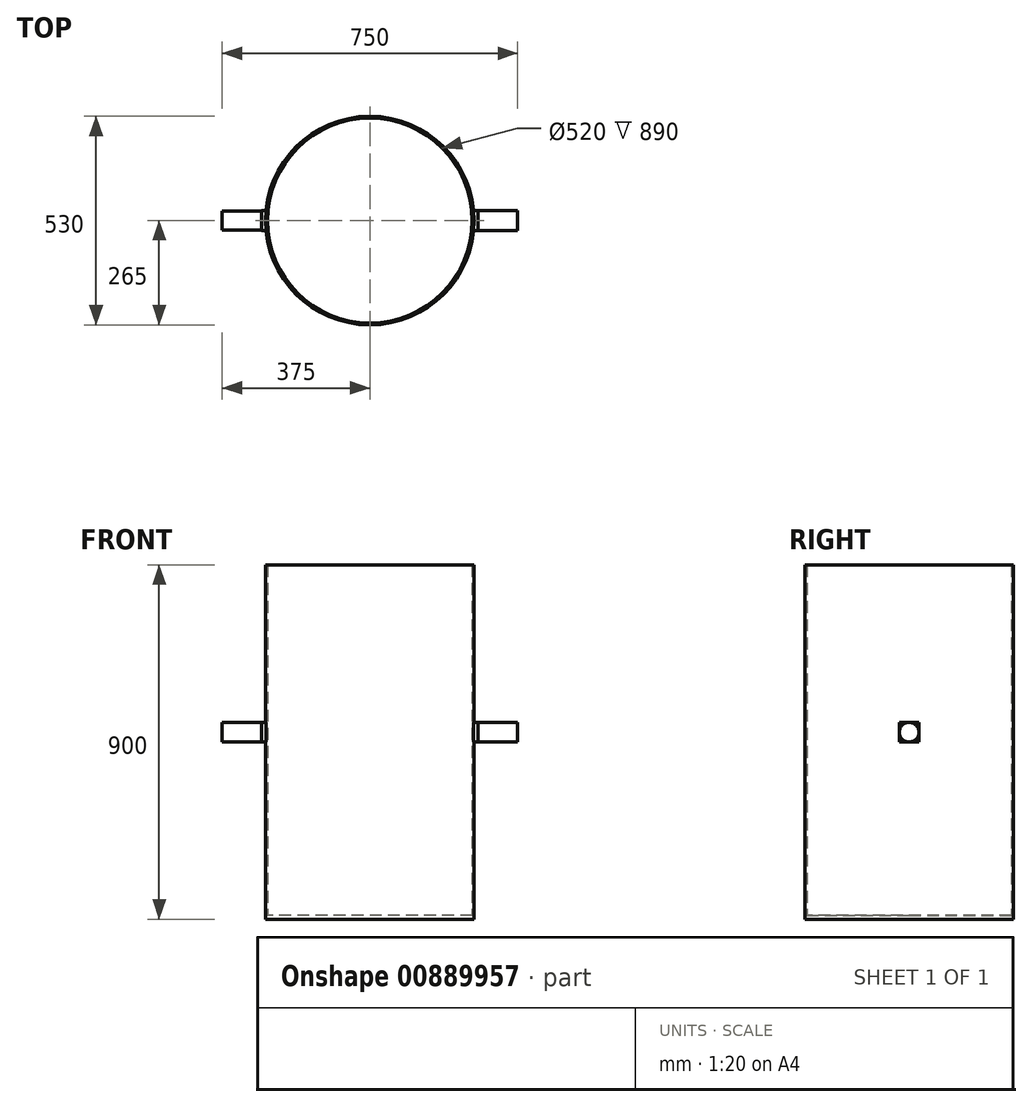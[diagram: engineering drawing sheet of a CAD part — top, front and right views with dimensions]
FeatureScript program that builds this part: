
annotation { "Feature Type Name" : "Feature", "Feature Type Description" : "" }
export const myFeature = defineFeature(function(context is Context, id is Id, definition is map)
    precondition{}
    {
        {
            var Q0;
            Q0=qCreatedBy(makeId("Top.planeOp"),FACE);
            var sketch = newSketch(context, id + "F0", { "sketchPlane" : qUnion([Q0])});
            skCircle(sketch, "E0", {"center": v(0, 0) * mm, "radius": 265 * mm});
            skLineSegment(sketch, "E1", {"start": v(265, 0) * mm, "end": v(275, 0) * mm});
            skLineSegment(sketch, "E2", {"start": v(275, 0) * mm, "end": v(275, 25) * mm});
            skLineSegment(sketch, "E3", {"start": v(275, 25) * mm, "end": v(263.82, 25) * mm});
            skLineSegment(sketch, "E4", {"start": v(275, 0) * mm, "end": v(275, -25) * mm});
            skLineSegment(sketch, "E5", {"start": v(275, -25) * mm, "end": v(263.82, -25) * mm});
            skLineSegment(sketch, "E6", {"start": v(-265, 0) * mm, "end": v(-275, 0) * mm});
            skLineSegment(sketch, "E7", {"start": v(-275, 0) * mm, "end": v(-275, 25) * mm});
            skLineSegment(sketch, "E8", {"start": v(-275, 0) * mm, "end": v(-275, -25) * mm});
            skLineSegment(sketch, "E9", {"start": v(-275, 25) * mm, "end": v(-263.82, 25) * mm});
            skLineSegment(sketch, "E10", {"start": v(-275, -25) * mm, "end": v(-263.82, -25) * mm});
            skCircle(sketch, "E11", {"center": v(0, 0) * mm, "radius": 260 * mm});
            skSolve(sketch);
        }
        {
            var Q0;
            Q0=makeQuery(id+"F0.imprint","IMPRINT",FACE,{"disambiguationData":[TD([[makeQuery(id+"F0.imprint","IMPRINT",EDGE,{"derivedFrom":sQuery(id+"F0.wireOp",EDGE,"E11")}),1.0]])]});
            var Q1;
            Q1=makeQuery(id+"F0.imprint","IMPRINT",FACE,{"disambiguationData":[TD([[makeQuery(id+"F0.imprint","IMPRINT",EDGE,{"derivedFrom":sQuery(id+"F0.wireOp",EDGE,"E11")}),-1.0]])]});
            extrude(context, id + "F1", {"entities" : qUnion([Q0, Q1]), "depth" : 10 * mm, "offsetDistance" : 25 * mm});
        }
        {
            var Q0;
            Q0=makeQuery(id+"F0.imprint","IMPRINT",FACE,{"disambiguationData":[TD([[makeQuery(id+"F0.imprint","IMPRINT",EDGE,{"derivedFrom":sQuery(id+"F0.wireOp",EDGE,"E11")}),-1.0]])]});
            extrude(context, id + "F2", {"entities" : qUnion([Q0]), "operationType" : NewBodyOperationType.ADD, "depth" : 900 * mm, "offsetDistance" : 25 * mm});
        }
        {
            var Q0;
            {var subQ0=sQuery(id+"F0.wireOp",EDGE,"E1");Q0=makeQuery(id+"F0.imprint","IMPRINT",FACE,{"disambiguationData":[TD([[makeQuery(id+"F0.imprint","IMPRINT",EDGE,{"derivedFrom":subQ0}),-1.0]])]});}
            var Q1;
            {var subQ0=sQuery(id+"F0.wireOp",EDGE,"E1");Q1=makeQuery(id+"F0.imprint","IMPRINT",FACE,{"disambiguationData":[TD([[makeQuery(id+"F0.imprint","IMPRINT",EDGE,{"derivedFrom":subQ0}),1.0]])]});}
            var Q2;
            {var subQ0=sQuery(id+"F0.wireOp",EDGE,"E6");Q2=makeQuery(id+"F0.imprint","IMPRINT",FACE,{"disambiguationData":[TD([[makeQuery(id+"F0.imprint","IMPRINT",EDGE,{"derivedFrom":subQ0}),-1.0]])]});}
            var Q3;
            {var subQ0=sQuery(id+"F0.wireOp",EDGE,"E6");Q3=makeQuery(id+"F0.imprint","IMPRINT",FACE,{"disambiguationData":[TD([[makeQuery(id+"F0.imprint","IMPRINT",EDGE,{"derivedFrom":subQ0}),1.0]])]});}
            extrude(context, id + "F3", {"entities" : qUnion([Q0, Q1, Q2, Q3]), "operationType" : NewBodyOperationType.ADD, "depth" : 500 * mm, "offsetDistance" : 25 * mm});
        }
        {
            var Q0;
            {var subQ0=sQuery(id+"F0.wireOp",EDGE,"E1");Q0=makeQuery(id+"F0.imprint","IMPRINT",FACE,{"disambiguationData":[TD([[makeQuery(id+"F0.imprint","IMPRINT",EDGE,{"derivedFrom":subQ0}),1.0]])]});}
            var Q1;
            {var subQ0=sQuery(id+"F0.wireOp",EDGE,"E1");Q1=makeQuery(id+"F0.imprint","IMPRINT",FACE,{"disambiguationData":[TD([[makeQuery(id+"F0.imprint","IMPRINT",EDGE,{"derivedFrom":subQ0}),-1.0]])]});}
            var Q2;
            {var subQ0=sQuery(id+"F0.wireOp",EDGE,"E6");Q2=makeQuery(id+"F0.imprint","IMPRINT",FACE,{"disambiguationData":[TD([[makeQuery(id+"F0.imprint","IMPRINT",EDGE,{"derivedFrom":subQ0}),-1.0]])]});}
            var Q3;
            {var subQ0=sQuery(id+"F0.wireOp",EDGE,"E6");Q3=makeQuery(id+"F0.imprint","IMPRINT",FACE,{"disambiguationData":[TD([[makeQuery(id+"F0.imprint","IMPRINT",EDGE,{"derivedFrom":subQ0}),1.0]])]});}
            extrude(context, id + "F4", {"entities" : qUnion([Q0, Q1, Q2, Q3]), "operationType" : NewBodyOperationType.REMOVE, "depth" : 450 * mm, "offsetDistance" : 25 * mm});
        }
        {
            var Q0;
            Q0=makeQuery(id+"F3.opExtrude","SWEPT_FACE",FACE,{"disambiguationData":[OSD([sQuery(id+"F0.wireOp",EDGE,"E7"),sQuery(id+"F0.wireOp",EDGE,"E8")])]});
            var sketch = newSketch(context, id + "F5", { "sketchPlane" : qUnion([Q0])});
            skLineSegment(sketch, "E12", {"start": v(-25, 500) * mm, "end": v(25, 500) * mm});
            skLineSegment(sketch, "E13", {"start": v(25, 500) * mm, "end": v(25, 450) * mm});
            skLineSegment(sketch, "E14", {"start": v(25, 450) * mm, "end": v(-25, 450) * mm});
            skLineSegment(sketch, "E15", {"start": v(-25, 450) * mm, "end": v(-25, 500) * mm});
            skCircle(sketch, "E16", {"center": v(0, 475) * mm, "radius": 24.53 * mm});
            skSolve(sketch);
        }
        {
            var Q0;
            Q0=makeQuery(id+"F5.imprint","IMPRINT",FACE,{"disambiguationData":[TD([[makeQuery(id+"F5.imprint","IMPRINT",EDGE,{"derivedFrom":sQuery(id+"F5.wireOp",EDGE,"E16")}),1.0]])]});
            extrude(context, id + "F6", {"entities" : qUnion([Q0]), "operationType" : NewBodyOperationType.ADD, "depth" : 100 * mm, "offsetDistance" : 25 * mm});
        }
        {
            var Q0;
            Q0=makeQuery(id+"F3.opExtrude","SWEPT_FACE",FACE,{"disambiguationData":[OSD([sQuery(id+"F0.wireOp",EDGE,"E2"),sQuery(id+"F0.wireOp",EDGE,"E4")])]});
            var sketch = newSketch(context, id + "F7", { "sketchPlane" : qUnion([Q0])});
            skLineSegment(sketch, "E17", {"start": v(-25, 500) * mm, "end": v(25, 450) * mm});
            skLineSegment(sketch, "E18", {"start": v(25, 450) * mm, "end": v(25, 500) * mm});
            skLineSegment(sketch, "E19", {"start": v(25, 500) * mm, "end": v(-25, 450) * mm});
            skCircle(sketch, "E20", {"center": v(0, 475) * mm, "radius": 25 * mm});
            skSolve(sketch);
        }
        {
            var Q0;
            {var subQ0=sQuery(id+"F7.wireOp",EDGE,"E19");var subQ1=sQuery(id+"F7.wireOp",EDGE,"E17");var subQ2=makeQuery(id+"F7.imprint","INTERSECT",VERTEX,{"derivedFrom":[subQ1,subQ0]});Q0=makeQuery(id+"F7.imprint","IMPRINT",FACE,{"disambiguationData":[TD([[makeQuery(id+"F7.imprint","IMPRINT",EDGE,{"disambiguationData":[TD([[subQ2,-1.0]])],"derivedFrom":subQ1}),1.0]])]});}
            var Q1;
            {var subQ0=sQuery(id+"F7.wireOp",EDGE,"E20");var subQ1=sQuery(id+"F7.wireOp",EDGE,"E17");var subQ2=makeQuery(id+"F7.imprint","INTERSECT",VERTEX,{"disambiguationData":[OD(0.0)],"derivedFrom":[subQ1,subQ0]});Q1=makeQuery(id+"F7.imprint","IMPRINT",FACE,{"disambiguationData":[TD([[makeQuery(id+"F7.imprint","IMPRINT",EDGE,{"disambiguationData":[TD([[subQ2,-1.0]])],"derivedFrom":subQ1}),1.0]])]});}
            var Q2;
            {var subQ0=sQuery(id+"F7.wireOp",EDGE,"E20");var subQ1=sQuery(id+"F7.wireOp",EDGE,"E17");var subQ2=makeQuery(id+"F7.imprint","INTERSECT",VERTEX,{"disambiguationData":[OD(0.0)],"derivedFrom":[subQ1,subQ0]});Q2=makeQuery(id+"F7.imprint","IMPRINT",FACE,{"disambiguationData":[TD([[makeQuery(id+"F7.imprint","IMPRINT",EDGE,{"disambiguationData":[TD([[subQ2,-1.0]])],"derivedFrom":subQ1}),-1.0]])]});}
            var Q3;
            {var subQ0=sQuery(id+"F7.wireOp",EDGE,"E19");var subQ1=sQuery(id+"F7.wireOp",EDGE,"E17");var subQ2=makeQuery(id+"F7.imprint","INTERSECT",VERTEX,{"derivedFrom":[subQ1,subQ0]});Q3=makeQuery(id+"F7.imprint","IMPRINT",FACE,{"disambiguationData":[TD([[makeQuery(id+"F7.imprint","IMPRINT",EDGE,{"disambiguationData":[TD([[subQ2,-1.0]])],"derivedFrom":subQ1}),-1.0]])]});}
            extrude(context, id + "F8", {"entities" : qUnion([Q0, Q1, Q2, Q3]), "operationType" : NewBodyOperationType.ADD, "depth" : 100 * mm, "offsetDistance" : 25 * mm});
        }
    });
